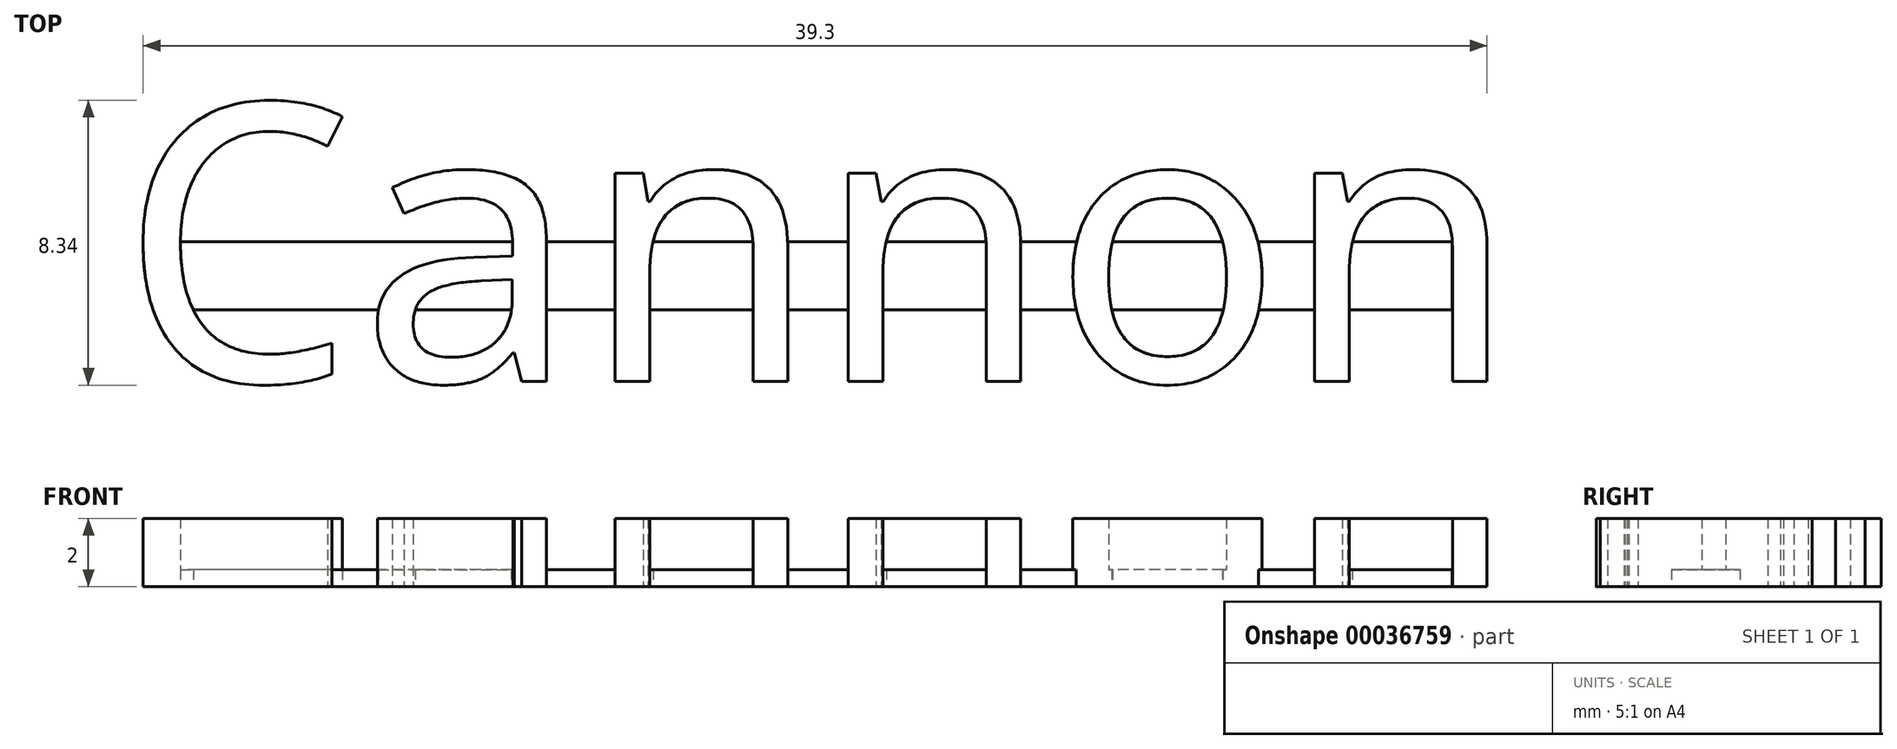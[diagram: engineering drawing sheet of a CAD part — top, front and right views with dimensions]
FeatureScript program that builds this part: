
annotation { "Feature Type Name" : "Feature", "Feature Type Description" : "" }
export const myFeature = defineFeature(function(context is Context, id is Id, definition is map)
    precondition{}
    {
        {
            var Q0;
            Q0=qCreatedBy(makeId("Top.planeOp"),FACE);
            var sketch = newSketch(context, id + "F0", { "sketchPlane" : qUnion([Q0])});
            skText(sketch, "E0", { "text": "Cannon", "fontName": "DroidSansMono.ttf"});
            const initialGuessF0  = {"E0": [-0.02, -0.00409, 1, 0, 0.00818]};
            skSetInitialGuess(sketch, initialGuessF0);
            skSolve(sketch);
        }
        {
            var Q0;
            Q0 = qSketchRegion(id + "F0", true);
            extrude(context, id + "F1", {"entities" : qUnion([Q0]), "depth" : 2 * mm});
        }
        {
            var Q0;
            Q0=qCreatedBy(makeId("Right.planeOp"),FACE);
            var sketch = newSketch(context, id + "F2", { "sketchPlane" : qUnion([Q0])});
            skLineSegment(sketch, "E1.bottom", {"start": v(0, 0) * mm, "end": v(-2, 0) * mm});
            skLineSegment(sketch, "E1.top", {"start": v(0, 0.5) * mm, "end": v(-2, 0.5) * mm});
            skLineSegment(sketch, "E1.left", {"start": v(0, 0) * mm, "end": v(0, 0.5) * mm});
            skLineSegment(sketch, "E1.right", {"start": v(-2, 0) * mm, "end": v(-2, 0.5) * mm});
            skLineSegment(sketch, "E2", {"start": v(-1, 0.5) * mm, "end": v(-1, 0) * mm, "construction": true});
            skSolve(sketch);
        }
        {
            var Q0;
            Q0 = qSketchRegion(id + "F2", true);
            extrude(context, id + "F3", {"entities" : qUnion([Q0]), "operationType" : NewBodyOperationType.ADD, "depth" : 19 * mm, "hasSecondDirection" : true, "secondDirectionOppositeDirection" : true, "secondDirectionDepth" : 19 * mm});
        }
        {
            var Q0;
            {var subQ0=sQuery(id+"F2.wireOp",EDGE,"E1.top");Q0=makeQuery(id+"F3.boolean.opBoolean","SPLIT",FACE,{"disambiguationData":[TD([makeQuery(id+"F1.opExtrude","SWEPT_FACE",FACE,{"disambiguationData":[OSD([sQuery(id+"F0.wireOp",EDGE,"E0.sketch_text.stroke-3")])]})])],"derivedFrom":makeQuery(id+"F3.opExtrude","SWEPT_FACE",FACE,{"disambiguationData":[OSD([subQ0])]})});}
            extrude(context, id + "F4", {"entities" : qUnion([Q0]), "operationType" : NewBodyOperationType.REMOVE, "oppositeDirection" : true, "depth" : 25 * mm});
        }
    });
